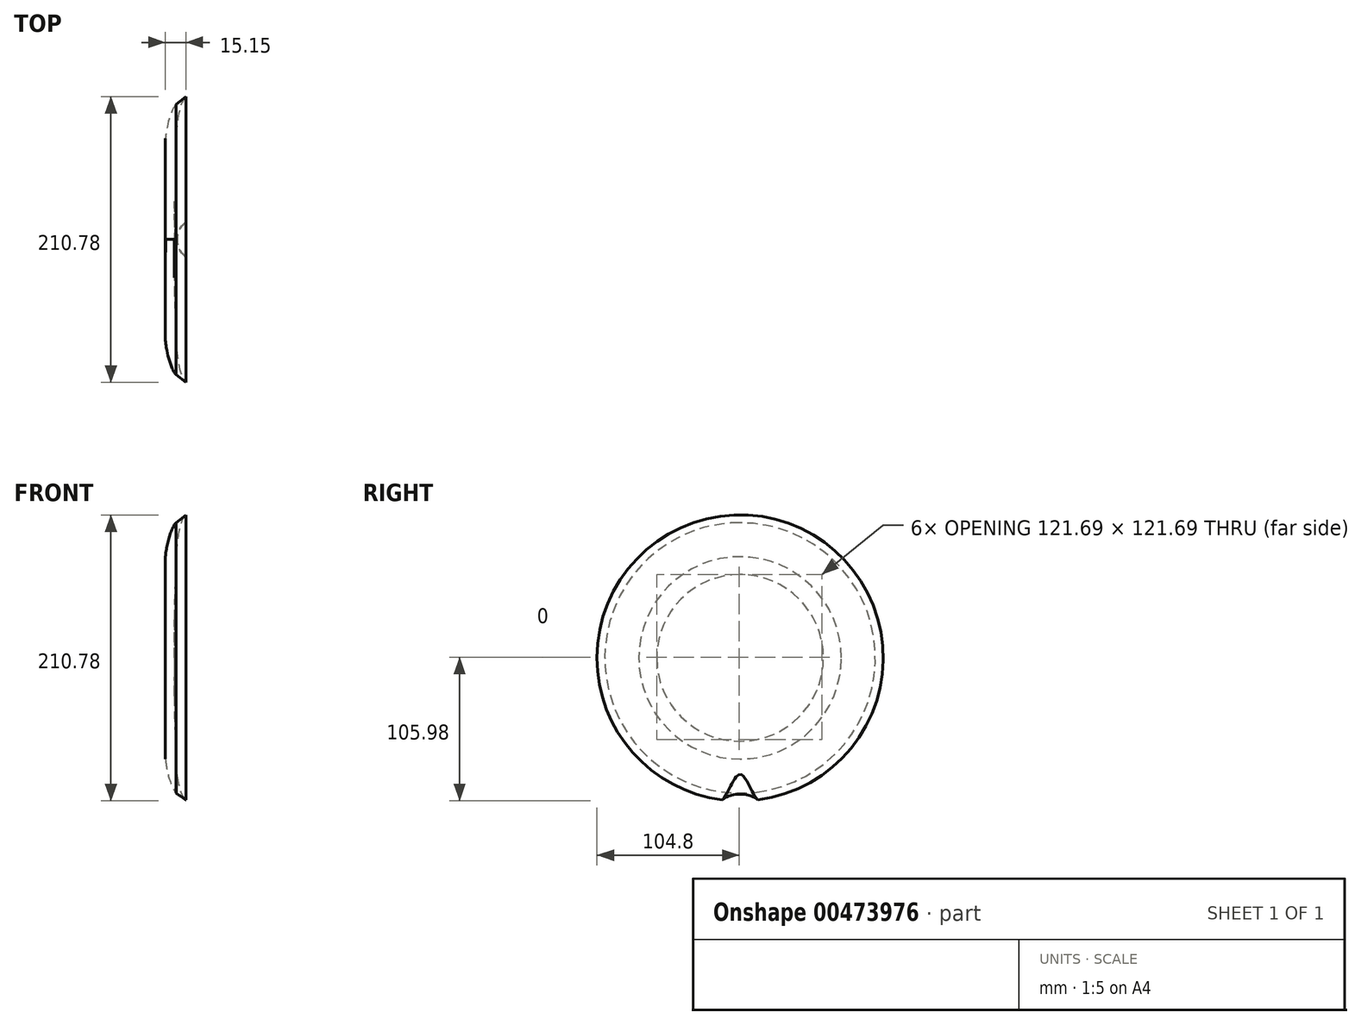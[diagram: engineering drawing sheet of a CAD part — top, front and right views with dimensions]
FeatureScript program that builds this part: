
annotation { "Feature Type Name" : "Feature", "Feature Type Description" : "" }
export const myFeature = defineFeature(function(context is Context, id is Id, definition is map)
    precondition{}
    {
        {
            var Q0;
            Q0=qCreatedBy(makeId("Top.planeOp"),FACE);
            var sketch = newSketch(context, id + "F0", { "sketchPlane" : qUnion([Q0])});
            skLineSegment(sketch, "E0", {"start": v(0, 0) * mm, "end": v(7.8, 0) * mm});
            skFitSpline(sketch, "E1", {"points": [v(7.8, 0) * mm, v(7.8, -68.69) * mm, v(7.8, -74.57) * mm, v(15.17, -105.42) * mm], "startDerivative": vector(-17.01, -150.27) * mm, "endDerivative": vector(47.51, -37.13) * mm});
            skFitSpline(sketch, "E2", {"points": [v(0, 0) * mm, v(0, -28.32) * mm, v(0, -61.43) * mm, v(0, -74.57) * mm, v(7.8, -99.6) * mm], "startDerivative": vector(6.55, -93.25) * mm, "endDerivative": vector(50.33, -59.47) * mm});
            skLineSegment(sketch, "E3", {"start": v(15.17, -105.42) * mm, "end": v(7.8, -99.6) * mm});
            skSolve(sketch);
        }
        {
            var Q0;
            Q0=makeQuery(id+"F0.imprint","IMPRINT",FACE,{"disambiguationData":[TD([[makeQuery(id+"F0.imprint","IMPRINT",EDGE,{"derivedFrom":sQuery(id+"F0.wireOp",EDGE,"E0")}),-1.0]])]});
            var Q1;
            Q1=sQuery(id+"F0.wireOp",EDGE,"E0");
            revolve(context, id + "F1", {"entities" : qUnion([Q0]), "axis" : qUnion([Q1]), "revolveType" : RevolveType.FULL});
        }
        {
            var Q0;
            Q0=qCreatedBy(makeId("Right.planeOp"),FACE);
            var sketch = newSketch(context, id + "F2", { "sketchPlane" : qUnion([Q0])});
            skCircle(sketch, "E4", {"center": v(0, 0) * mm, "radius": 137.67 * mm});
            skSolve(sketch);
        }
        {
            var Q0;
            Q0 = qSketchRegion(id + "F2", true);
            extrude(context, id + "F3", {"entities" : qUnion([Q0]), "operationType" : NewBodyOperationType.REMOVE, "oppositeDirection" : true, "depth" : 1.52 * mm});
        }
        {
            var Q0;
            Q0=qCreatedBy(makeId("Top.planeOp"),FACE);
            var sketch = newSketch(context, id + "F4", { "sketchPlane" : qUnion([Q0])});
            skCircle(sketch, "E5", {"center": v(25.23, 0) * mm, "radius": 16.48 * mm});
            skSolve(sketch);
        }
        {
            var Q0;
            Q0 = qSketchRegion(id + "F4", true);
            extrude(context, id + "F5", {"entities" : qUnion([Q0]), "operationType" : NewBodyOperationType.REMOVE, "endBound" : BoundingType.THROUGH_ALL, "oppositeDirection" : true, "depth" : 25.4 * mm});
        }
    });
